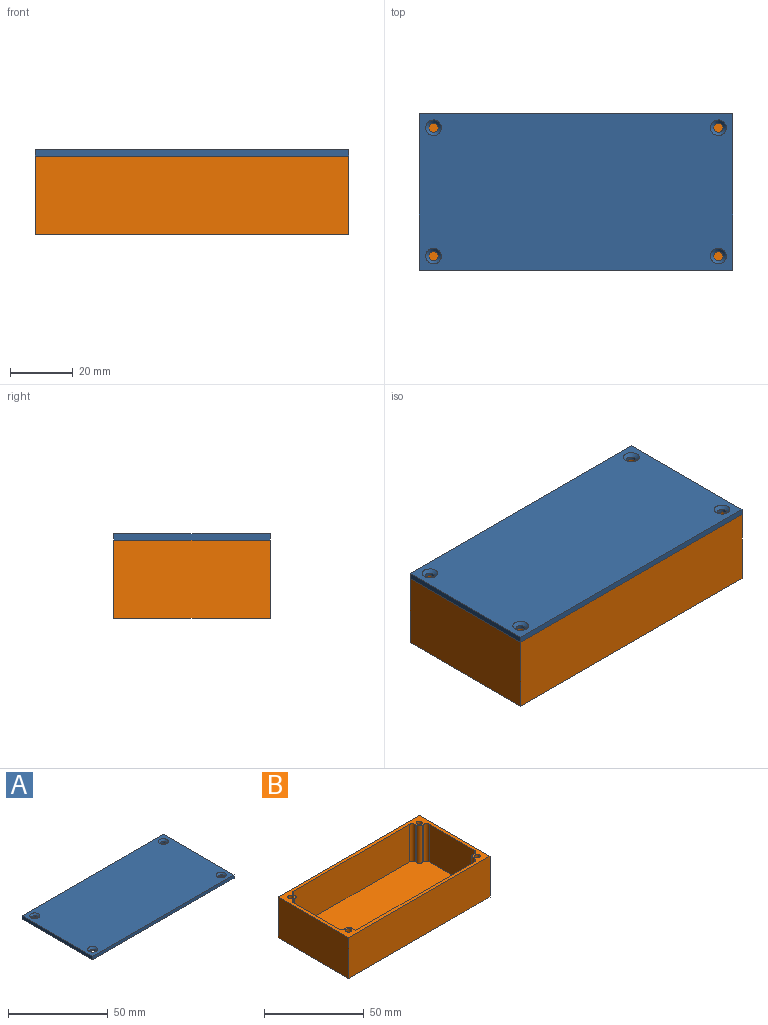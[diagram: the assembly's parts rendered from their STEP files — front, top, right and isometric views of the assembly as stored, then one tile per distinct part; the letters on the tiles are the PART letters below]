
ASSEMBLY  parts=2 mates=1
PART A: 14 faces, bbox 100x50x2 mm
  f0: plane 100x2mm, normal (0,1,0), area 200mm2, adj f1,f7,f8,f9
  f1: plane 50x2mm, normal (-1,0,0), area 100mm2, adj f0,f2,f8,f9
  f2: plane 100x2mm, normal (0,-1,0), area 200mm2, adj f1,f7,f8,f9
  f3: cylinder r=1.5mm len=3mm, axis (0,0,-1), area 9.4mm2, adj f9,f13
  f4: cylinder r=1.5mm len=3mm, axis (0,0,-1), area 9.4mm2, adj f9,f12
  f5: cylinder r=1.5mm len=3mm, axis (0,0,-1), area 9.4mm2, adj f9,f11
  f6: cylinder r=1.5mm len=3mm, axis (0,0,-1), area 9.4mm2, adj f9,f10
  f7: plane 50x2mm, normal (1,0,0), area 100mm2, adj f0,f2,f8,f9
  f8: plane 100x50mm, normal (0,0,1), area 4921.5mm2, adj f0,f1,f2,f7,f10,f11,f12,f13
  f9: plane 100x50mm, normal (0,0,-1), area 4971.7mm2, adj f0,f1,f2,f3,f4,f5,f6,f7
  f10: cone r=1.5mm half-angle=45deg, axis (0,0,1), area 17.8mm2, adj f6,f8
  f11: cone r=1.5mm half-angle=45deg, axis (0,0,1), area 17.8mm2, adj f5,f8
  f12: cone r=1.5mm half-angle=45deg, axis (0,0,1), area 17.8mm2, adj f4,f8
  f13: cone r=1.5mm half-angle=45deg, axis (0,0,1), area 17.8mm2, adj f3,f8
PART B: 38 faces, bbox 100x50x25 mm
  f0: plane 96x46mm, normal (0,0,1), area 4313.4mm2, adj f1,f2,f3,f4,f11,f12,f13,f14
  f1: plane 84x23mm, normal (0,1,0), area 1932mm2, adj f0,f5,f16,f27
  f2: plane 32x23mm, normal (-1,0,0), area 736mm2, adj f0,f5,f29,f32
  f3: plane 32x23mm, normal (1,0,0), area 736mm2, adj f0,f5,f31,f37
  f4: plane 82x23mm, normal (0,-1,0), area 1886mm2, adj f0,f5,f33,f35
  f5: plane 100x50mm, normal (0,0,1), area 658.3mm2, adj f1,f2,f3,f4,f6,f7,f8,f9
  f6: plane 100x25mm, normal (0,1,0), area 2500mm2, adj f5,f7,f9,f10
  f7: plane 50x25mm, normal (-1,0,0), area 1250mm2, adj f5,f6,f8,f10
  f8: plane 100x25mm, normal (0,-1,0), area 2500mm2, adj f5,f7,f9,f10
  f9: plane 50x25mm, normal (1,0,0), area 1250mm2, adj f5,f6,f8,f10
  f10: plane 100x50mm, normal (0,0,-1), area 5000mm2, adj f6,f7,f8,f9
  f11: plane 23x1mm, normal (0,-1,0), area 23mm2, adj f0,f5,f36,f37
  f12: plane 23x1mm, normal (1,0,0), area 23mm2, adj f0,f5,f35,f36
  f13: plane 23x1mm, normal (0,-1,0), area 23mm2, adj f0,f5,f32,f34
  f14: plane 23x1mm, normal (-1,0,0), area 23mm2, adj f0,f5,f33,f34
  f15: plane 23x1mm, normal (0,1,0), area 23mm2, adj f0,f5,f30,f31
  f16: plane 23x3mm, normal (1,0,0), area 69mm2, adj f0,f1,f5,f30
  f17: plane 23x1mm, normal (0,1,0), area 23mm2, adj f0,f5,f28,f29
  f18: plane 23x1mm, normal (-1,0,0), area 23mm2, adj f0,f5,f27,f28
  f19: cylinder r=1.5mm len=23mm, axis (0,0,1), area 216.8mm2, adj f5,f20
  f20: plane 3x3mm, normal (0,0,1), area 7.1mm2, adj f19
  f21: cylinder r=1.5mm len=23mm, axis (0,0,1), area 216.8mm2, adj f5,f22
  f22: plane 3x3mm, normal (0,0,1), area 7.1mm2, adj f21
  f23: cylinder r=1.5mm len=23mm, axis (0,0,1), area 216.8mm2, adj f5,f24
  f24: plane 3x3mm, normal (0,0,1), area 7.1mm2, adj f23
  f25: cylinder r=1.5mm len=23mm, axis (0,0,1), area 216.8mm2, adj f5,f26
  f26: plane 3x3mm, normal (0,0,1), area 7.1mm2, adj f25
  f27: cylinder r=2mm len=23mm, axis (0,0,1), area 72.3mm2, adj f0,f1,f5,f18
  f28: cylinder r=2mm len=23mm, axis (0,0,1), area 72.3mm2, adj f0,f5,f17,f18
  f29: cylinder r=2mm len=23mm, axis (0,0,1), area 72.3mm2, adj f0,f2,f5,f17
  f30: cylinder r=2mm len=23mm, axis (0,0,1), area 72.3mm2, adj f0,f5,f15,f16
  f31: cylinder r=2mm len=23mm, axis (0,0,1), area 72.3mm2, adj f0,f3,f5,f15
  f32: cylinder r=2mm len=23mm, axis (0,0,-1), area 72.3mm2, adj f0,f2,f5,f13
  f33: cylinder r=2mm len=23mm, axis (0,0,1), area 72.3mm2, adj f0,f4,f5,f14
  f34: cylinder r=2mm len=23mm, axis (0,0,1), area 72.3mm2, adj f0,f5,f13,f14
  f35: cylinder r=2mm len=23mm, axis (0,0,-1), area 72.3mm2, adj f0,f4,f5,f12
  f36: cylinder r=2mm len=23mm, axis (0,0,1), area 72.3mm2, adj f0,f5,f11,f12
  f37: cylinder r=2mm len=23mm, axis (0,0,-1), area 72.3mm2, adj f0,f3,f5,f11
PLACE A t=(-94.36,-47.32,-4.08)mm
PLACE B t=(-94.36,-47.32,-29.08)mm
MATE fastened B.f23 <-> A.f5  axis (0,0,1) through (-48.86,-67.82,-4.08)mm
